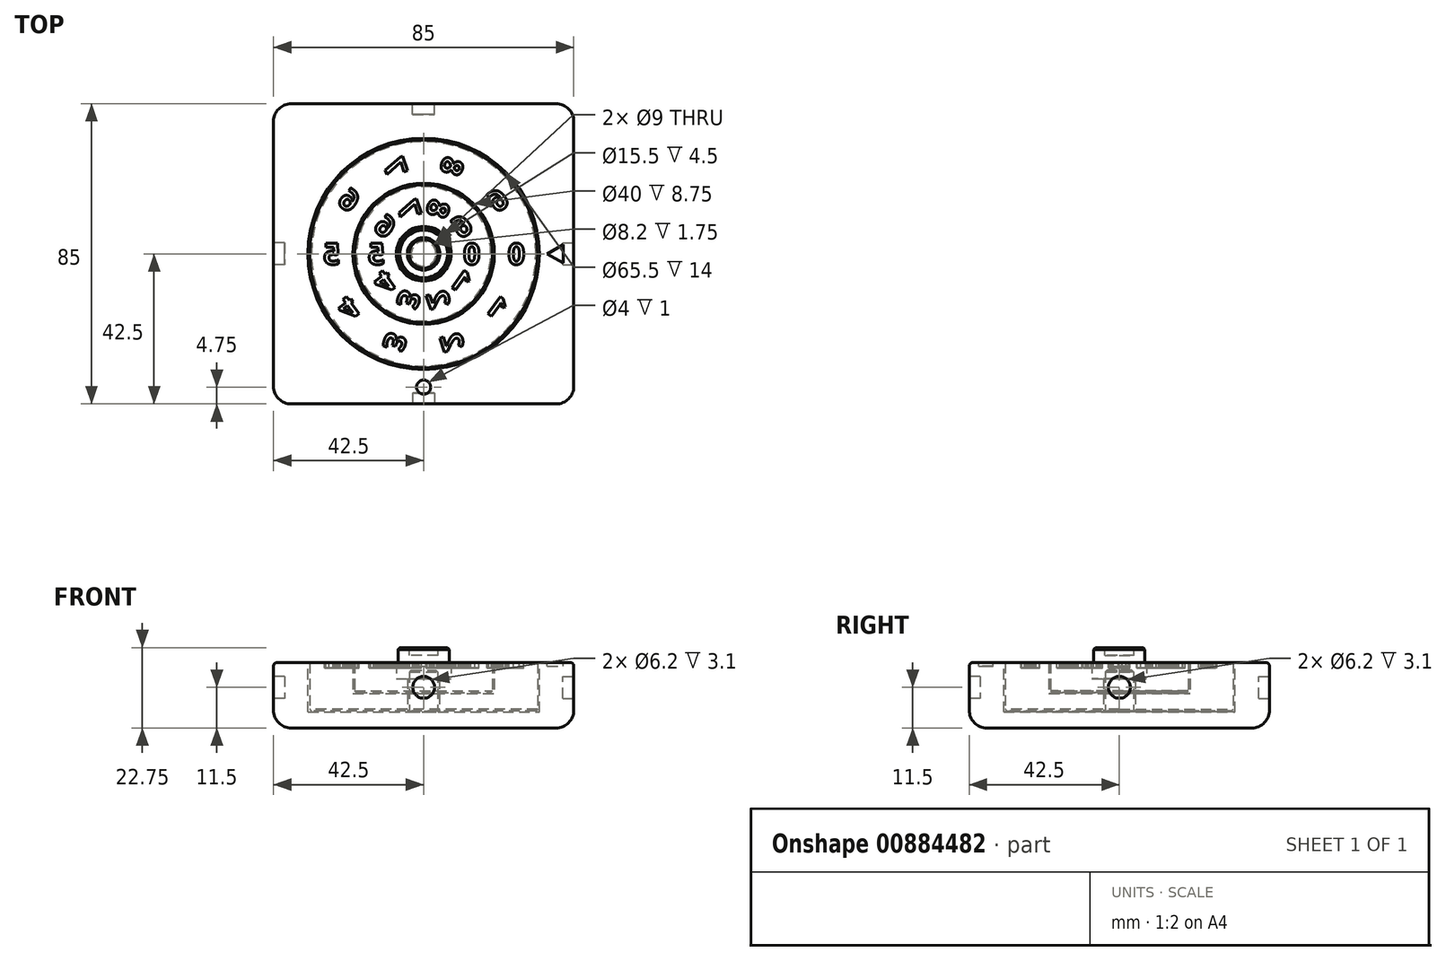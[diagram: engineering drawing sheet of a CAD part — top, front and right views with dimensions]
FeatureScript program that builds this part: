
annotation { "Feature Type Name" : "Feature", "Feature Type Description" : "" }
export const myFeature = defineFeature(function(context is Context, id is Id, definition is map)
    precondition{}
    {
        {
            var Q0;
            Q0=qCreatedBy(makeId("Top.planeOp"),FACE);
            var sketch = newSketch(context, id + "F0", { "sketchPlane" : qUnion([Q0])});
            skLineSegment(sketch, "E0.bottom", {"start": v(-42.5, 42.5) * mm, "end": v(42.5, 42.5) * mm});
            skLineSegment(sketch, "E0.top", {"start": v(-42.5, -42.5) * mm, "end": v(42.5, -42.5) * mm});
            skLineSegment(sketch, "E0.left", {"start": v(-42.5, 42.5) * mm, "end": v(-42.5, -42.5) * mm});
            skLineSegment(sketch, "E0.right", {"start": v(42.5, 42.5) * mm, "end": v(42.5, -42.5) * mm});
            skLineSegment(sketch, "E1", {"start": v(-42.5, 0) * mm, "end": v(42.5, 0) * mm, "construction": true});
            skLineSegment(sketch, "E2", {"start": v(0, -42.5) * mm, "end": v(0, 42.5) * mm, "construction": true});
            skCircle(sketch, "E3", {"center": v(0, -37.75) * mm, "radius": 2 * mm});
            skCircle(sketch, "E4", {"center": v(0, 0) * mm, "radius": 32.75 * mm});
            skSolve(sketch);
        }
        {
            assignVariable(context, id + "F1", {"name" : "h", "anyValue" : 18.5});
        }
        {
            assignVariable(context, id + "F2", {"name" : "d", "anyValue" : 14});
        }
        {
            var Q0;
            Q0=makeQuery(id+"F0.imprint","IMPRINT",FACE,{"disambiguationData":[TD([[makeQuery(id+"F0.imprint","IMPRINT",EDGE,{"derivedFrom":sQuery(id+"F0.wireOp",EDGE,"TAnjNuv1-8zZz-IdIO-9YnW-rZbYslCo22iK.bottom")}),-1.0]])]});
            var Q1;
            Q1=makeQuery(id+"F0.imprint","IMPRINT",FACE,{"disambiguationData":[TD([[makeQuery(id+"F0.imprint","IMPRINT",EDGE,{"derivedFrom":sQuery(id+"F0.wireOp",EDGE,"E0.bottom")}),-1.0]])]});
            var Q2;
            Q2=makeQuery(id+"F0.imprint","IMPRINT",FACE,{"disambiguationData":[TD([[makeQuery(id+"F0.imprint","IMPRINT",EDGE,{"derivedFrom":sQuery(id+"F0.wireOp",EDGE,"2ee7e992-b2ee-4d81-b33c-59d4d4482344.0.2.0")}),1.0]])]});
            var Q3;
            Q3=makeQuery(id+"F0.imprint","IMPRINT",FACE,{"disambiguationData":[TD([[makeQuery(id+"F0.imprint","IMPRINT",EDGE,{"derivedFrom":sQuery(id+"F0.wireOp",EDGE,"2ee7e992-b2ee-4d81-b33c-59d4d4482344.0.3.0")}),1.0]])]});
            var Q4;
            Q4=makeQuery(id+"F0.imprint","IMPRINT",FACE,{"disambiguationData":[TD([[makeQuery(id+"F0.imprint","IMPRINT",EDGE,{"derivedFrom":sQuery(id+"F0.wireOp",EDGE,"2ee7e992-b2ee-4d81-b33c-59d4d4482344.0.1.0")}),1.0]])]});
            var Q5;
            Q5=makeQuery(id+"F0.imprint","IMPRINT",FACE,{"disambiguationData":[TD([[makeQuery(id+"F0.imprint","IMPRINT",EDGE,{"derivedFrom":sQuery(id+"F0.wireOp",EDGE,"f406dc69-17c4-4892-9ae8-b8d3958ef0eb.0.1.2")}),1.0]])]});
            var Q6;
            Q6=makeQuery(id+"F0.imprint","IMPRINT",FACE,{"disambiguationData":[TD([[makeQuery(id+"F0.imprint","IMPRINT",EDGE,{"derivedFrom":sQuery(id+"F0.wireOp",EDGE,"f406dc69-17c4-4892-9ae8-b8d3958ef0eb.0.2.2")}),1.0]])]});
            var Q7;
            Q7=makeQuery(id+"F0.imprint","IMPRINT",FACE,{"disambiguationData":[TD([[makeQuery(id+"F0.imprint","IMPRINT",EDGE,{"derivedFrom":sQuery(id+"F0.wireOp",EDGE,"f406dc69-17c4-4892-9ae8-b8d3958ef0eb.0.3.2")}),1.0]])]});
            var Q8;
            Q8=makeQuery(id+"F0.imprint","IMPRINT",FACE,{"disambiguationData":[TD([[makeQuery(id+"F0.imprint","IMPRINT",EDGE,{"derivedFrom":sQuery(id+"F0.wireOp",EDGE,"E3")}),1.0]])]});
            var Q9;
            Q9=makeQuery(id+"F0.imprint","IMPRINT",FACE,{"disambiguationData":[TD([[makeQuery(id+"F0.imprint","IMPRINT",EDGE,{"derivedFrom":sQuery(id+"F0.wireOp",EDGE,"E4")}),1.0]])]});
            var Q10;
            Q10=makeQuery(id+"F0.imprint","IMPRINT",FACE,{"disambiguationData":[TD([[makeQuery(id+"F0.imprint","IMPRINT",EDGE,{"derivedFrom":sQuery(id+"F0.wireOp",EDGE,"VVb0DQBK-mlck-W3en-msYo-o1gmNoqsQ1XS")}),1.0]])]});
            extrude(context, id + "F3", {"entities" : qUnion([Q0, Q1, Q2, Q3, Q4, Q5, Q6, Q7, Q8, Q9, Q10]), "depth" : (getVariable(context, 'h')) * mm, "offsetDistance" : 25 * mm});
        }
        {
            var Q0;
            Q0=makeQuery(id+"F0.imprint","IMPRINT",FACE,{"disambiguationData":[TD([[makeQuery(id+"F0.imprint","IMPRINT",EDGE,{"derivedFrom":sQuery(id+"F0.wireOp",EDGE,"E4")}),1.0]])]});
            extrude(context, id + "F4", {"entities" : qUnion([Q0]), "operationType" : NewBodyOperationType.REMOVE, "depth" : (getVariable(context, 'd')) * mm, "offsetDistance" : 25 * mm});
        }
        {
            var Q0;
            Q0=makeQuery(id+"F3.opExtrude","CAP_FACE",FACE,{"disambiguationData":[OSD([sQuery(id+"F0.wireOp",EDGE,"E0.bottom"),sQuery(id+"F0.wireOp",EDGE,"E0.top"),sQuery(id+"F0.wireOp",EDGE,"E0.left"),sQuery(id+"F0.wireOp",EDGE,"E0.right")])],"isStart":false});
            var Q1;
            Q1=makeQuery(id+"F3.opExtrude","SWEPT_EDGE",EDGE,{"disambiguationData":[OSD([sQuery(id+"F0.wireOp",EDGE,"E0.bottom"),sQuery(id+"F0.wireOp",EDGE,"E0.right")])]});
            var Q2;
            Q2=makeQuery(id+"F3.opExtrude","SWEPT_EDGE",EDGE,{"disambiguationData":[OSD([sQuery(id+"F0.wireOp",EDGE,"E0.bottom"),sQuery(id+"F0.wireOp",EDGE,"E0.left")])]});
            var Q3;
            Q3=makeQuery(id+"F3.opExtrude","SWEPT_EDGE",EDGE,{"disambiguationData":[OSD([sQuery(id+"F0.wireOp",EDGE,"E0.top"),sQuery(id+"F0.wireOp",EDGE,"E0.left")])]});
            var Q4;
            Q4=makeQuery(id+"F3.opExtrude","SWEPT_EDGE",EDGE,{"disambiguationData":[OSD([sQuery(id+"F0.wireOp",EDGE,"E0.top"),sQuery(id+"F0.wireOp",EDGE,"E0.right")])]});
            fillet(context, id + "F5", {"entities" : qUnion([Q0, Q1, Q2, Q3, Q4]), "radius" : 5 * mm, "tangentPropagation" : true, "allowEdgeOverflow" : false});
        }
        {
            var Q0;
            Q0=makeQuery(id+"F3.opExtrude","CAP_EDGE",EDGE,{"disambiguationData":[OSD([sQuery(id+"F0.wireOp",EDGE,"E0.left")])],"isStart":true});
            fillet(context, id + "F6", {"entities" : qUnion([Q0]), "radius" : 1 * mm, "tangentPropagation" : true, "allowEdgeOverflow" : false});
        }
        {
            var Q0;
            Q0=makeQuery(id+"F3.opExtrude","SWEPT_FACE",FACE,{"disambiguationData":[OSD([sQuery(id+"F0.wireOp",EDGE,"E0.top")])]});
            var sketch = newSketch(context, id + "F7", { "sketchPlane" : qUnion([Q0])});
            skCircle(sketch, "E5", {"center": v(0, 7) * mm, "radius": 3.1 * mm});
            skSolve(sketch);
        }
        {
            var Q0;
            Q0=makeQuery(id+"F7.imprint","IMPRINT",FACE,{"disambiguationData":[TD([[makeQuery(id+"F7.imprint","IMPRINT",EDGE,{"derivedFrom":sQuery(id+"F7.wireOp",EDGE,"E5")}),1.0]])]});
            extrude(context, id + "F8", {"entities" : qUnion([Q0]), "operationType" : NewBodyOperationType.REMOVE, "oppositeDirection" : true, "depth" : 3.1 * mm, "offsetDistance" : 25 * mm});
        }
        {
            var Q0;
            Q0=makeQuery(id+"F3.opExtrude","SWEPT_FACE",FACE,{"disambiguationData":[OSD([sQuery(id+"F0.wireOp",EDGE,"E0.bottom")])]});
            var sketch = newSketch(context, id + "F9", { "sketchPlane" : qUnion([Q0])});
            skCircle(sketch, "E6", {"center": v(0, 7) * mm, "radius": 3.1 * mm});
            skSolve(sketch);
        }
        {
            var Q0;
            Q0=makeQuery(id+"F9.imprint","IMPRINT",FACE,{"disambiguationData":[TD([[makeQuery(id+"F9.imprint","IMPRINT",EDGE,{"derivedFrom":sQuery(id+"F9.wireOp",EDGE,"E6")}),1.0]])]});
            extrude(context, id + "F10", {"entities" : qUnion([Q0]), "operationType" : NewBodyOperationType.REMOVE, "oppositeDirection" : true, "depth" : 3.1 * mm, "offsetDistance" : 25 * mm});
        }
        {
            var Q0;
            Q0=makeQuery(id+"F3.opExtrude","SWEPT_FACE",FACE,{"disambiguationData":[OSD([sQuery(id+"F0.wireOp",EDGE,"E0.left")])]});
            var sketch = newSketch(context, id + "F11", { "sketchPlane" : qUnion([Q0])});
            skCircle(sketch, "E7", {"center": v(0, 7) * mm, "radius": 3.1 * mm});
            skSolve(sketch);
        }
        {
            var Q0;
            Q0=makeQuery(id+"F11.imprint","IMPRINT",FACE,{"disambiguationData":[TD([[makeQuery(id+"F11.imprint","IMPRINT",EDGE,{"derivedFrom":sQuery(id+"F11.wireOp",EDGE,"E7")}),1.0]])]});
            extrude(context, id + "F12", {"entities" : qUnion([Q0]), "operationType" : NewBodyOperationType.REMOVE, "oppositeDirection" : true, "depth" : 3.1 * mm, "offsetDistance" : 25 * mm});
        }
        {
            var Q0;
            Q0=makeQuery(id+"F3.opExtrude","SWEPT_FACE",FACE,{"disambiguationData":[OSD([sQuery(id+"F0.wireOp",EDGE,"E0.right")])]});
            var sketch = newSketch(context, id + "F13", { "sketchPlane" : qUnion([Q0])});
            skCircle(sketch, "E8", {"center": v(0, 7) * mm, "radius": 3.1 * mm});
            skSolve(sketch);
        }
        {
            var Q0;
            Q0=makeQuery(id+"F13.imprint","IMPRINT",FACE,{"disambiguationData":[TD([[makeQuery(id+"F13.imprint","IMPRINT",EDGE,{"derivedFrom":sQuery(id+"F13.wireOp",EDGE,"E8")}),1.0]])]});
            extrude(context, id + "F14", {"entities" : qUnion([Q0]), "operationType" : NewBodyOperationType.REMOVE, "oppositeDirection" : true, "depth" : 3.1 * mm, "offsetDistance" : 25 * mm});
        }
        {
            var Q0;
            Q0=makeQuery(id+"F0.imprint","IMPRINT",FACE,{"disambiguationData":[TD([[makeQuery(id+"F0.imprint","IMPRINT",EDGE,{"derivedFrom":sQuery(id+"F0.wireOp",EDGE,"E3")}),1.0]])]});
            var Q1;
            Q1=sQuery(id+"F0.wireOp",EDGE,"E3");
            extrude(context, id + "F15", {"entities" : qUnion([Q0]), "operationType" : NewBodyOperationType.REMOVE, "surfaceEntities" : qUnion([Q1]), "depth" : 1 * mm, "offsetDistance" : 25 * mm});
        }
        {
            var Q0;
            Q0=qCreatedBy(makeId("Front.planeOp"),FACE);
            var sketch = newSketch(context, id + "F16", { "sketchPlane" : qUnion([Q0])});
            skLineSegment(sketch, "E9", {"start": v(0, 13.75) * mm, "end": v(0, 8.75) * mm, "construction": true});
            skLineSegment(sketch, "E10", {"start": v(-20, 0) * mm, "end": v(-32.25, 0) * mm});
            skLineSegment(sketch, "E11", {"start": v(-32.25, 0) * mm, "end": v(-32.25, 13.75) * mm});
            skLineSegment(sketch, "E12", {"start": v(-32.25, 13.75) * mm, "end": v(-4.5, 13.75) * mm});
            skLineSegment(sketch, "E13", {"start": v(-20, 0) * mm, "end": v(-20, 8.75) * mm});
            skLineSegment(sketch, "E14", {"start": v(-20, 8.75) * mm, "end": v(-4.5, 8.75) * mm});
            skLineSegment(sketch, "E15", {"start": v(-4.5, 13.75) * mm, "end": v(-4.5, 8.75) * mm});
            skSolve(sketch);
        }
        {
            var Q0;
            Q0=makeQuery(id+"F16.imprint","IMPRINT",FACE,{"disambiguationData":[TD([[makeQuery(id+"F16.imprint","IMPRINT",EDGE,{"derivedFrom":sQuery(id+"F16.wireOp",EDGE,"E10")}),-1.0]])]});
            var Q1;
            Q1=qConstructionFilter(qBodyType(qCreatedBy(id+"F16",EDGE),BodyType.WIRE),ConstructionObject.NO);
            var Q2;
            Q2=sQuery(id+"F16.wireOp",EDGE,"E9");
            revolve(context, id + "F17", {"surfaceOperationType" : NewSurfaceOperationType.NEW, "entities" : qUnion([Q0]), "surfaceEntities" : qUnion([Q1]), "axis" : qUnion([Q2]), "revolveType" : RevolveType.FULL});
        }
        {
            var Q0;
            Q0=qCreatedBy(makeId("Front.planeOp"),FACE);
            var sketch = newSketch(context, id + "F18", { "sketchPlane" : qUnion([Q0])});
            skLineSegment(sketch, "E16", {"start": v(-4.5, 8.5) * mm, "end": v(-19.5, 8.5) * mm});
            skLineSegment(sketch, "E17", {"start": v(-19.5, 8.5) * mm, "end": v(-19.5, 0) * mm});
            skLineSegment(sketch, "E18", {"start": v(-19.5, 0) * mm, "end": v(-7.75, 0) * mm});
            skLineSegment(sketch, "E19", {"start": v(-7.75, 0) * mm, "end": v(-7.75, 4.5) * mm});
            skLineSegment(sketch, "E20", {"start": v(-7.75, 4.5) * mm, "end": v(-4.5, 4.5) * mm});
            skLineSegment(sketch, "E21", {"start": v(-4.5, 4.5) * mm, "end": v(-4.5, 8.5) * mm});
            skPoint(sketch, "E22.orphan", {"position": v(0, 8.5) * mm});
            skLineSegment(sketch, "E23", {"start": v(0, 19.44) * mm, "end": v(0, -7.38) * mm, "construction": true});
            skSolve(sketch);
        }
        {
            var Q0;
            Q0=makeQuery(id+"F18.imprint","IMPRINT",FACE,{"disambiguationData":[TD([[makeQuery(id+"F18.imprint","IMPRINT",EDGE,{"derivedFrom":sQuery(id+"F18.wireOp",EDGE,"E16")}),1.0]])]});
            var Q1;
            Q1=sQuery(id+"F18.wireOp",EDGE,"E23");
            revolve(context, id + "F19", {"surfaceOperationType" : NewSurfaceOperationType.NEW, "entities" : qUnion([Q0]), "axis" : qUnion([Q1]), "revolveType" : RevolveType.FULL});
        }
        {
            var Q0;
            Q0=makeQuery(id+"F0.imprint","IMPRINT",FACE,{"disambiguationData":[TD([[makeQuery(id+"F0.imprint","IMPRINT",EDGE,{"derivedFrom":sQuery(id+"F0.wireOp",EDGE,"E0.bottom")}),-1.0]])]});
            var sketch = newSketch(context, id + "F20", { "sketchPlane" : qUnion([Q0])});
            skLineSegment(sketch, "E24", {"start": v(0, 0) * mm, "end": v(13.5, 0) * mm, "construction": true});
            skLineSegment(sketch, "E25.1.0", {"start": v(0, 0) * mm, "end": v(32.76, 23.8) * mm, "construction": true});
            skLineSegment(sketch, "E25.2.0", {"start": v(0, 0) * mm, "end": v(12.51, 38.5) * mm, "construction": true});
            skLineSegment(sketch, "E25.3.0", {"start": v(0, 0) * mm, "end": v(-12.51, 38.5) * mm, "construction": true});
            skLineSegment(sketch, "E25.4.0", {"start": v(0, 0) * mm, "end": v(-32.76, 23.8) * mm, "construction": true});
            skLineSegment(sketch, "E25.5.0", {"start": v(0, 0) * mm, "end": v(-13.5, 0) * mm, "construction": true});
            skLineSegment(sketch, "E25.6.0", {"start": v(0, 0) * mm, "end": v(-21.14, -15.36) * mm, "construction": true});
            skLineSegment(sketch, "E25.7.0", {"start": v(0, 0) * mm, "end": v(-12.51, -38.5) * mm, "construction": true});
            skLineSegment(sketch, "E25.8.0", {"start": v(0, 0) * mm, "end": v(8.07, -24.85) * mm, "construction": true});
            skLineSegment(sketch, "E25.9.0", {"start": v(0, 0) * mm, "end": v(21.14, -15.36) * mm, "construction": true});
            skPoint(sketch, "E25.center", {"position": v(0, 0) * mm});
            skCircle(sketch, "E26", {"center": v(0, 0) * mm, "radius": 32.5 * mm, "construction": true});
            skCircle(sketch, "E27", {"center": v(0, 0) * mm, "radius": 19.75 * mm, "construction": true});
            skText(sketch, "E28", { "text": "0", "fontName": "OpenSans-Bold.ttf"});
            skLineSegment(sketch, "E29", {"start": v(-26.12, 0) * mm, "end": v(-28.62, 0) * mm, "construction": true});
            skLineSegment(sketch, "E30", {"start": v(-21.14, -15.36) * mm, "end": v(-32.76, -23.8) * mm, "construction": true});
            skArc(sketch, "E31", {"start": v(-21.14, 15.36) * mm, "mid": v(-24.85, -8.07) * mm, "end": v(-8.07, -24.85) * mm, "construction": true});
            skArc(sketch, "E32", {"start": v(-8.07, 24.85) * mm, "mid": v(-15.36, 21.14) * mm, "end": v(-21.14, 15.36) * mm, "construction": true});
            skArc(sketch, "E33", {"start": v(8.07, 24.85) * mm, "mid": v(0, 26.12) * mm, "end": v(-8.07, 24.85) * mm, "construction": true});
            skArc(sketch, "E34", {"start": v(21.14, 15.36) * mm, "mid": v(15.36, 21.14) * mm, "end": v(8.07, 24.85) * mm, "construction": true});
            skArc(sketch, "E35", {"start": v(26.12, 0) * mm, "mid": v(24.85, 8.07) * mm, "end": v(21.14, 15.36) * mm, "construction": true});
            skLineSegment(sketch, "E36", {"start": v(21.14, -15.36) * mm, "end": v(32.76, -23.8) * mm, "construction": true});
            skLineSegment(sketch, "E37", {"start": v(8.07, -24.85) * mm, "end": v(12.51, -38.5) * mm, "construction": true});
            skArc(sketch, "E38", {"start": v(-8.07, -24.85) * mm, "mid": v(15.36, -21.14) * mm, "end": v(26.12, 0) * mm, "construction": true});
            skText(sketch, "E39", { "text": "1", "fontName": "OpenSans-Bold.ttf"});
            skLineSegment(sketch, "E40", {"start": v(-21.14, -15.36) * mm, "end": v(-22.75, -16.53) * mm, "construction": true});
            skText(sketch, "E41", { "text": "2", "fontName": "OpenSans-Bold.ttf"});
            skLineSegment(sketch, "E42", {"start": v(-8.07, -24.85) * mm, "end": v(-8.85, -27.24) * mm, "construction": true});
            skText(sketch, "E43", { "text": "3", "fontName": "OpenSans-Bold.ttf"});
            skLineSegment(sketch, "E44", {"start": v(8.07, -24.85) * mm, "end": v(8.84, -27.21) * mm, "construction": true});
            skText(sketch, "E45", { "text": "4", "fontName": "OpenSans-Bold.ttf"});
            skLineSegment(sketch, "E46", {"start": v(23.23, -16.87) * mm, "end": v(21.14, -15.36) * mm, "construction": true});
            skText(sketch, "E47", { "text": "5\n", "fontName": "OpenSans-Bold.ttf"});
            skLineSegment(sketch, "E48", {"start": v(26.13, 0) * mm, "end": v(23.66, 0) * mm, "construction": true});
            skText(sketch, "E49", { "text": "6\n", "fontName": "OpenSans-Bold.ttf"});
            skLineSegment(sketch, "E50", {"start": v(21.14, 15.36) * mm, "end": v(23.17, 16.83) * mm, "construction": true});
            skText(sketch, "E51", { "text": "7", "fontName": "OpenSans-Bold.ttf"});
            skLineSegment(sketch, "E52", {"start": v(8.07, 24.85) * mm, "end": v(8.85, 27.24) * mm, "construction": true});
            skText(sketch, "E53", { "text": "8", "fontName": "OpenSans-Bold.ttf"});
            skLineSegment(sketch, "E54", {"start": v(-8.85, 27.23) * mm, "end": v(-8.07, 24.85) * mm, "construction": true});
            skText(sketch, "E55", { "text": "9", "fontName": "OpenSans-Bold.ttf"});
            skLineSegment(sketch, "E56", {"start": v(-23.16, 16.83) * mm, "end": v(-21.14, 15.36) * mm, "construction": true});
            skText(sketch, "E57", { "text": "5\n", "fontName": "OpenSans-Bold.ttf"});
            skLineSegment(sketch, "E58", {"start": v(13.5, 0) * mm, "end": v(11.04, 0) * mm, "construction": true});
            skCircle(sketch, "E59", {"center": v(0, 0) * mm, "radius": 7.5 * mm, "construction": true});
            skCircle(sketch, "E60", {"center": v(0, 0) * mm, "radius": 19.5 * mm, "construction": true});
            skLineSegment(sketch, "E61", {"start": v(13.5, 0) * mm, "end": v(40.49, 0) * mm, "construction": true});
            skArc(sketch, "E62", {"start": v(10.92, 7.94) * mm, "mid": v(7.94, 10.92) * mm, "end": v(4.17, 12.84) * mm, "construction": true});
            skArc(sketch, "E63", {"start": v(10.92, -7.94) * mm, "mid": v(13.5, 0) * mm, "end": v(10.92, 7.94) * mm, "construction": true});
            skArc(sketch, "E64", {"start": v(4.17, -12.84) * mm, "mid": v(7.94, -10.92) * mm, "end": v(10.92, -7.94) * mm, "construction": true});
            skArc(sketch, "E65", {"start": v(-4.17, -12.84) * mm, "mid": v(0, -13.5) * mm, "end": v(4.17, -12.84) * mm, "construction": true});
            skArc(sketch, "E66", {"start": v(4.17, 12.84) * mm, "mid": v(0, 13.5) * mm, "end": v(-4.17, 12.84) * mm, "construction": true});
            skArc(sketch, "E67", {"start": v(-4.17, 12.84) * mm, "mid": v(-7.94, 10.92) * mm, "end": v(-10.92, 7.94) * mm, "construction": true});
            skArc(sketch, "E68", {"start": v(-10.92, 7.94) * mm, "mid": v(-13.5, 0) * mm, "end": v(-10.92, -7.94) * mm, "construction": true});
            skLineSegment(sketch, "E69", {"start": v(-13.5, 0) * mm, "end": v(-40.49, 0) * mm, "construction": true});
            skArc(sketch, "E70", {"start": v(-10.92, -7.94) * mm, "mid": v(-7.94, -10.92) * mm, "end": v(-4.17, -12.84) * mm, "construction": true});
            skText(sketch, "E71", { "text": "6\n", "fontName": "OpenSans-Bold.ttf"});
            skLineSegment(sketch, "E72", {"start": v(10.92, 7.94) * mm, "end": v(12.96, 9.41) * mm, "construction": true});
            skText(sketch, "E73", { "text": "7", "fontName": "OpenSans-Bold.ttf"});
            skLineSegment(sketch, "E74", {"start": v(4.17, 12.84) * mm, "end": v(4.95, 15.23) * mm, "construction": true});
            skText(sketch, "E75", { "text": "8", "fontName": "OpenSans-Bold.ttf"});
            skLineSegment(sketch, "E76", {"start": v(-4.95, 15.22) * mm, "end": v(-4.17, 12.84) * mm, "construction": true});
            skText(sketch, "E77", { "text": "9", "fontName": "OpenSans-Bold.ttf"});
            skLineSegment(sketch, "E78", {"start": v(-12.95, 9.4) * mm, "end": v(-10.92, 7.94) * mm, "construction": true});
            skText(sketch, "E79", { "text": "0", "fontName": "OpenSans-Bold.ttf"});
            skLineSegment(sketch, "E80", {"start": v(-13.5, 0) * mm, "end": v(-16, 0) * mm, "construction": true});
            skText(sketch, "E81", { "text": "1", "fontName": "OpenSans-Bold.ttf"});
            skLineSegment(sketch, "E82", {"start": v(-10.92, -7.94) * mm, "end": v(-12.53, -9.1) * mm, "construction": true});
            skText(sketch, "E83", { "text": "2", "fontName": "OpenSans-Bold.ttf"});
            skLineSegment(sketch, "E84", {"start": v(-4.17, -12.84) * mm, "end": v(-4.95, -15.23) * mm, "construction": true});
            skText(sketch, "E85", { "text": "3", "fontName": "OpenSans-Bold.ttf"});
            skLineSegment(sketch, "E86", {"start": v(4.17, -12.84) * mm, "end": v(4.94, -15.2) * mm, "construction": true});
            skText(sketch, "E87", { "text": "4", "fontName": "OpenSans-Bold.ttf"});
            skLineSegment(sketch, "E88", {"start": v(13.01, -9.45) * mm, "end": v(10.92, -7.94) * mm, "construction": true});
            const initialGuessF20  = {"E28": [-0.02862, -0.003, 1, 0, 0.006], "E39": [-0.02098, -0.01895, 0.80902, 0.58779, 0.006], "E41": [-0.006, -0.02817, 0.30902, 0.95106, 0.006], "E43": [0.0117, -0.02629, -0.30902, 0.95106, 0.006], "E45": [0.02499, -0.01445, -0.80902, 0.58779, 0.006], "E47": [0.02366, -0.003, 1, 0, 0.006], "E49": [0.02086, 0.01145, 0.80902, 0.58779, 0.006], "E51": [0.01015, 0.02153, 0.30902, 0.95106, 0.006], "E53": [-0.00445, 0.0234, -0.30902, 0.95106, 0.006], "E55": [-0.01735, 0.01631, -0.80902, 0.58779, 0.006], "E57": [0.01104, -0.003, 1, 0, 0.006], "E71": [0.01065, 0.00403, 0.80902, 0.58779, 0.006], "E73": [0.00625, 0.00952, 0.30902, 0.95106, 0.006], "E75": [-0.00054, 0.01138, -0.30902, 0.95106, 0.006], "E77": [-0.00713, 0.0089, -0.80902, 0.58779, 0.006], "E79": [-0.016, -0.003, 1, 0, 0.006], "E81": [-0.01077, -0.01153, 0.80902, 0.58779, 0.006], "E83": [-0.0021, -0.01616, 0.30902, 0.95106, 0.006], "E85": [0.0078, -0.01428, -0.30902, 0.95106, 0.006], "E87": [0.01478, -0.00703, -0.80902, 0.58779, 0.006]};
            skSetInitialGuess(sketch, initialGuessF20);
            skSolve(sketch);
        }
        {
            var Q0;
            Q0=qSketchRegion(id+"F20",true);
            extrude(context, id + "F21", {"entities" : qUnion([Q0]), "operationType" : NewBodyOperationType.REMOVE, "depth" : 1.5 * mm, "offsetDistance" : 25 * mm});
        }
        {
            var Q0;
            Q0=qSketchRegion(id+"F20",true);
            extrude(context, id + "F22", {"entities" : qUnion([Q0]), "operationType" : NewBodyOperationType.REMOVE, "depth" : 1.5 * mm, "offsetDistance" : 25 * mm});
        }
        {
            var Q0;
            Q0=qCreatedBy(makeId("Front.planeOp"),FACE);
            var sketch = newSketch(context, id + "F23", { "sketchPlane" : qUnion([Q0])});
            skLineSegment(sketch, "E89", {"start": v(0, 2.2) * mm, "end": v(4, 2.2) * mm});
            skLineSegment(sketch, "E90", {"start": v(4, 2.2) * mm, "end": v(4, 18.5) * mm});
            skLineSegment(sketch, "E91", {"start": v(4, 18.5) * mm, "end": v(0, 18.5) * mm});
            skLineSegment(sketch, "E92", {"start": v(0, 18.5) * mm, "end": v(0, 2.2) * mm});
            skSolve(sketch);
        }
        {
            var Q0;
            Q0=qCreatedBy(makeId("Front.planeOp"),FACE);
            var sketch = newSketch(context, id + "F24", { "sketchPlane" : qUnion([Q0])});
            skLineSegment(sketch, "E93", {"start": v(0, 0) * mm, "end": v(7.25, 0) * mm});
            skLineSegment(sketch, "E94", {"start": v(7.25, 0) * mm, "end": v(7.25, 4.25) * mm});
            skLineSegment(sketch, "E95", {"start": v(7.25, 4.25) * mm, "end": v(4.1, 4.25) * mm});
            skLineSegment(sketch, "E96", {"start": v(4.1, 2) * mm, "end": v(4.1, 4.25) * mm});
            skLineSegment(sketch, "E97", {"start": v(4.1, 2) * mm, "end": v(0, 2) * mm});
            skLineSegment(sketch, "E98", {"start": v(0, 2) * mm, "end": v(0, 0) * mm});
            skSolve(sketch);
        }
        {
            var Q0;
            Q0 = qSketchRegion(id + "F24", true);
            var Q1;
            Q1=sQuery(id+"F23.wireOp",EDGE,"E92");
            revolve(context, id + "F25", {"surfaceOperationType" : NewSurfaceOperationType.NEW, "entities" : qUnion([Q0]), "axis" : qUnion([Q1]), "revolveType" : RevolveType.FULL});
        }
        {
            var Q0;
            Q0=makeQuery(id+"F23.imprint","IMPRINT",FACE,{"disambiguationData":[TD([[makeQuery(id+"F23.imprint","IMPRINT",EDGE,{"derivedFrom":sQuery(id+"F23.wireOp",EDGE,"E89")}),1.0]])]});
            var Q1;
            Q1=sQuery(id+"F23.wireOp",EDGE,"E92");
            revolve(context, id + "F26", {"operationType" : NewBodyOperationType.ADD, "surfaceOperationType" : NewSurfaceOperationType.NEW, "entities" : qUnion([Q0]), "axis" : qUnion([Q1]), "revolveType" : RevolveType.FULL});
        }
        {
            var Q0;
            Q0=makeQuery(id+"F3.opExtrude","SWEPT_BODY",BODY,{"disambiguationData":[OSD([sQuery(id+"F0.wireOp",EDGE,"E0.bottom"),sQuery(id+"F0.wireOp",EDGE,"E0.top"),sQuery(id+"F0.wireOp",EDGE,"E0.left"),sQuery(id+"F0.wireOp",EDGE,"E0.right")])]});
            var Q1;
            Q1=makeQuery(id+"F17.opRevolve","SWEPT_BODY",BODY,{"disambiguationData":[OSD([sQuery(id+"F16.wireOp",EDGE,"E10"),sQuery(id+"F16.wireOp",EDGE,"E11"),sQuery(id+"F16.wireOp",EDGE,"Aie8hkyw-sGVv-VvHk-Vuon-uzybwQ6q8sCs"),sQuery(id+"F16.wireOp",EDGE,"5iYQVoPB-RYPC-Byc3-8Mwj-mYxfChCvoJpU"),sQuery(id+"F16.wireOp",EDGE,"E12"),sQuery(id+"F16.wireOp",EDGE,"5d5cb49a-536e-4c3b-a1ce-db0e1b689141.filletArc"),sQuery(id+"F16.wireOp",EDGE,"a17601ce-2253-42fe-bf70-d0b3573d03f8.filletArc"),sQuery(id+"F16.wireOp",EDGE,"f7d95dab-f2fc-45d6-a469-ac977952581e.filletArc"),sQuery(id+"F16.wireOp",EDGE,"E13"),sQuery(id+"F16.wireOp",EDGE,"56zeP9kV-tJSd-Hlcb-SpQa-tqnfpjGjU1X5"),sQuery(id+"F16.wireOp",EDGE,"ahT2uenx-uqqy-WISf-5FU7-xqfa2nJREz1Q"),sQuery(id+"F16.wireOp",EDGE,"E14"),sQuery(id+"F16.wireOp",EDGE,"c427969b-4ba0-4108-9a38-1b870a68cabf.filletArc"),sQuery(id+"F16.wireOp",EDGE,"3970b9d9-4525-4822-90a2-07cffd8828e4.filletArc"),sQuery(id+"F16.wireOp",EDGE,"44d3b4ed-8f24-4f23-ab81-0a878a1fe82f.filletArc"),sQuery(id+"F16.wireOp",EDGE,"E15")])]});
            var Q2;
            Q2=makeQuery(id+"F19.opRevolve","SWEPT_BODY",BODY,{"disambiguationData":[OSD([sQuery(id+"F18.wireOp",EDGE,"E16"),sQuery(id+"F18.wireOp",EDGE,"W4LSucIC-1C3w-Vb3v-Y5OA-wqxnhI604Acs"),sQuery(id+"F18.wireOp",EDGE,"RQdPJZLI-iYu5-S2u7-tIFJ-PkMc2e3CjjGh"),sQuery(id+"F18.wireOp",EDGE,"E17"),sQuery(id+"F18.wireOp",EDGE,"E18"),sQuery(id+"F18.wireOp",EDGE,"E19"),sQuery(id+"F18.wireOp",EDGE,"E20"),sQuery(id+"F18.wireOp",EDGE,"E21"),sQuery(id+"F18.wireOp",EDGE,"caf7a765-5534-4870-827b-03466f1c99e3.filletArc"),sQuery(id+"F18.wireOp",EDGE,"dd2b0f7d-4639-499b-b715-159063f6e088.filletArc"),sQuery(id+"F18.wireOp",EDGE,"7f4fc2b8-c080-4429-a952-9433392ce116.filletArc"),sQuery(id+"F18.wireOp",EDGE,"d3ce06f0-3ce8-42c3-862a-95c5991aedac.filletArc")])]});
            var Q3;
            Q3=sQuery(id+"F0.wireOp",EDGE,"E2");
            var Q4;
            Q4=sQuery(id+"F0.wireOp",EDGE,"E2");
            transform(context, id + "F27", {"entities" : qUnion([Q0, Q1, Q2]), "transformType" : TransformType.ROTATION, "transformAxis" : qUnion([Q4]), "angle" : 180 * degree, "makeCopy" : false});
        }
        {
            var Q0;
            Q0=makeQuery(id+"F0.imprint","IMPRINT",FACE,{"disambiguationData":[TD([[makeQuery(id+"F0.imprint","IMPRINT",EDGE,{"derivedFrom":sQuery(id+"F0.wireOp",EDGE,"E0.bottom")}),-1.0]])]});
            var sketch = newSketch(context, id + "F28", { "sketchPlane" : qUnion([Q0])});
            skCircle(sketch, "E99.cCircle", {"center": v(38, 0) * mm, "radius": 1.5 * mm, "construction": true});
            skLineSegment(sketch, "E99.0", {"start": v(39.5, 2.6) * mm, "end": v(39.5, -2.6) * mm});
            skLineSegment(sketch, "E99.1", {"start": v(39.5, -2.6) * mm, "end": v(35, 0) * mm});
            skLineSegment(sketch, "E99.2", {"start": v(35, 0) * mm, "end": v(39.5, 2.6) * mm});
            skPoint(sketch, "E99.0.midPoint", {"position": v(39.5, 0) * mm});
            skSolve(sketch);
        }
        {
            var Q0;
            Q0=qSketchRegion(id+"F28",true);
            extrude(context, id + "F29", {"entities" : qUnion([Q0]), "operationType" : NewBodyOperationType.REMOVE, "oppositeDirection" : true, "depth" : 1 * mm, "offsetDistance" : 25 * mm});
        }
        {
            var Q0;
            Q0=makeQuery(id+"F26.opRevolve","SWEPT_EDGE",EDGE,{"disambiguationData":[OSD([sQuery(id+"F23.wireOp",EDGE,"E89"),sQuery(id+"F23.wireOp",EDGE,"E90")])]});
            var Q1;
            Q1=makeQuery(id+"F25.opRevolve","SWEPT_FACE",FACE,{"disambiguationData":[OSD([sQuery(id+"F24.wireOp",EDGE,"E95")])]});
            var Q2;
            Q2=makeQuery(id+"F19.opRevolve","SWEPT_EDGE",EDGE,{"disambiguationData":[OSD([sQuery(id+"F18.wireOp",EDGE,"E16"),sQuery(id+"F18.wireOp",EDGE,"E17")])]});
            var Q3;
            Q3=makeQuery(id+"F17.opRevolve","SWEPT_EDGE",EDGE,{"disambiguationData":[OSD([sQuery(id+"F16.wireOp",EDGE,"E11"),sQuery(id+"F16.wireOp",EDGE,"E12")])]});
            chamfer(context, id + "F30", {"entities" : qUnion([Q0, Q1, Q2, Q3]), "width" : .5 * mm, "tangentPropagation" : true});
        }
    });
